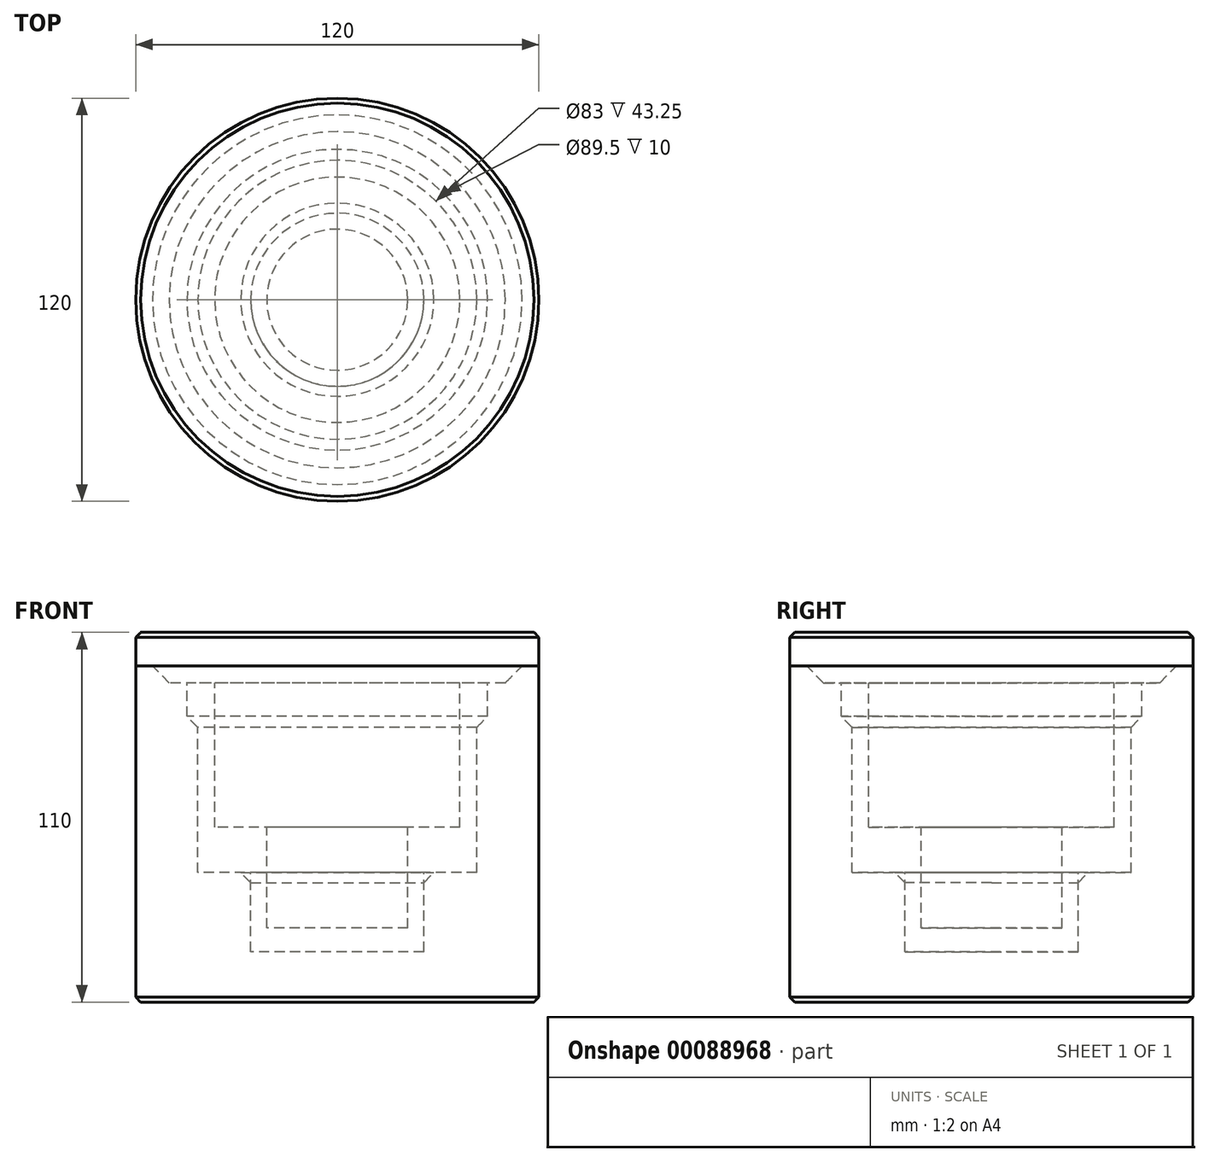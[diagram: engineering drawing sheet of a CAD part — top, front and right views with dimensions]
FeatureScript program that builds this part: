
annotation { "Feature Type Name" : "Feature", "Feature Type Description" : "" }
export const myFeature = defineFeature(function(context is Context, id is Id, definition is map)
    precondition{}
    {
        {
            var Q0;
            Q0=qCreatedBy(makeId("Front.planeOp"),FACE);
            var sketch = newSketch(context, id + "F0", { "sketchPlane" : qUnion([Q0])});
            skLineSegment(sketch, "E0.bottom", {"start": v(60, 47.5) * mm, "end": v(-60, 47.5) * mm});
            skLineSegment(sketch, "E0.top", {"start": v(60, -47.5) * mm, "end": v(-60, -47.5) * mm});
            skLineSegment(sketch, "E0.left", {"start": v(60, 47.5) * mm, "end": v(60, -47.5) * mm});
            skLineSegment(sketch, "E0.right", {"start": v(-60, 47.5) * mm, "end": v(-60, -47.5) * mm});
            skPoint(sketch, "E0.middle", {"position": v(0, 0) * mm});
            skLineSegment(sketch, "E1", {"start": v(0, 121.28) * mm, "end": v(0, -93.9) * mm});
            skLineSegment(sketch, "E2.top", {"start": v(25.75, -32.5) * mm, "end": v(-25.75, -32.5) * mm});
            skLineSegment(sketch, "E2.left", {"start": v(41.5, 32.5) * mm, "end": v(41.5, -9) * mm});
            skLineSegment(sketch, "E2.right", {"start": v(-41.5, 32.5) * mm, "end": v(-41.5, -9) * mm});
            skLineSegment(sketch, "E3", {"start": v(-41.5, 32.5) * mm, "end": v(-41.5, 47.5) * mm});
            skLineSegment(sketch, "E4", {"start": v(41.5, 30.56) * mm, "end": v(41.5, 47.5) * mm});
            skLineSegment(sketch, "E5", {"start": v(-60, 37.5) * mm, "end": v(60, 37.5) * mm});
            skLineSegment(sketch, "E6", {"start": v(-44.75, 47.5) * mm, "end": v(-44.75, 37.5) * mm});
            skLineSegment(sketch, "E7", {"start": v(44.75, 47.5) * mm, "end": v(44.75, 37.5) * mm});
            skLineSegment(sketch, "E8.top", {"start": v(21, -25.5) * mm, "end": v(-21, -25.5) * mm});
            skLineSegment(sketch, "E8.left", {"start": v(36.5, 25.5) * mm, "end": v(36.5, 4.5) * mm});
            skLineSegment(sketch, "E8.right", {"start": v(-36.5, 25.5) * mm, "end": v(-36.5, 4.5) * mm});
            skLineSegment(sketch, "E9", {"start": v(-36.5, 25.5) * mm, "end": v(-36.5, 47.5) * mm});
            skLineSegment(sketch, "E10", {"start": v(36.5, 25.5) * mm, "end": v(36.5, 47.5) * mm});
            skLineSegment(sketch, "E11", {"start": v(-60, 47.5) * mm, "end": v(-60, 62.5) * mm});
            skLineSegment(sketch, "E12", {"start": v(-60, 62.5) * mm, "end": v(60, 62.5) * mm});
            skLineSegment(sketch, "E13", {"start": v(60, 62.5) * mm, "end": v(60, 47.5) * mm});
            skPoint(sketch, "E14.orphan", {"position": v(0, 65.26) * mm});
            skLineSegment(sketch, "E15", {"start": v(-44.75, 37.5) * mm, "end": v(-41.5, 34.25) * mm});
            skPoint(sketch, "E16", {"position": v(-41.5, 40) * mm});
            skPoint(sketch, "E17.end.orphan", {"position": v(-46.38, 47.5) * mm});
            skPoint(sketch, "E18.end.orphan", {"position": v(-60, 52.5) * mm});
            skPoint(sketch, "E19.MirrorCS.end.orphan", {"position": v(46.38, 47.5) * mm});
            skPoint(sketch, "E20.MirrorCS.end.orphan", {"position": v(60, 52.5) * mm});
            skLineSegment(sketch, "E21.top", {"start": v(21, 25.5) * mm, "end": v(-21, 25.5) * mm});
            skLineSegment(sketch, "E21.left", {"start": v(21, -25.5) * mm, "end": v(21, 25.5) * mm});
            skLineSegment(sketch, "E21.right", {"start": v(-21, -25.5) * mm, "end": v(-21, 25.5) * mm});
            skLineSegment(sketch, "E22", {"start": v(-36.5, 4.5) * mm, "end": v(36.5, 4.5) * mm});
            skPoint(sketch, "E23.orphan", {"position": v(-36.5, -25.5) * mm});
            skPoint(sketch, "E24.orphan", {"position": v(36.5, -25.5) * mm});
            skLineSegment(sketch, "E25", {"start": v(-41.5, -9) * mm, "end": v(-25.75, -9) * mm});
            skLineSegment(sketch, "E26", {"start": v(-25.75, -9) * mm, "end": v(-25.75, -32.5) * mm});
            skLineSegment(sketch, "E27.MirrorCS", {"start": v(41.5, -9) * mm, "end": v(25.75, -9) * mm});
            skLineSegment(sketch, "E28.MirrorCS", {"start": v(25.75, -9) * mm, "end": v(25.75, -32.5) * mm});
            skPoint(sketch, "E29.orphan", {"position": v(-41.5, -32.5) * mm});
            skPoint(sketch, "E30.orphan", {"position": v(41.5, -32.5) * mm});
            skLineSegment(sketch, "E31", {"start": v(-60, 52.5) * mm, "end": v(-55, 52.5) * mm});
            skLineSegment(sketch, "E32", {"start": v(-55, 52.5) * mm, "end": v(-50, 47.5) * mm});
            skSolve(sketch);
        }
        {
            var Q0;
            {var subQ4=sQuery(id+"F0.wireOp",EDGE,"E18");Q0=makeQuery(id+"F0.imprint","IMPRINT",FACE,{"disambiguationData":[TD([[makeQuery(id+"F0.imprint","IMPRINT",EDGE,{"derivedFrom":subQ4}),1.0]])]});}
            var Q1;
            {var subQ3=sQuery(id+"F0.wireOp",EDGE,"E6");Q1=makeQuery(id+"F0.imprint","IMPRINT",FACE,{"disambiguationData":[TD([[makeQuery(id+"F0.imprint","IMPRINT",EDGE,{"derivedFrom":subQ3}),-1.0]])]});}
            var Q2;
            {var subQ10=sQuery(id+"F0.wireOp",EDGE,"E15");Q2=makeQuery(id+"F0.imprint","IMPRINT",FACE,{"disambiguationData":[TD([[makeQuery(id+"F0.imprint","IMPRINT",EDGE,{"derivedFrom":subQ10}),-1.0]])]});}
            var Q3;
            {var subQ4=sQuery(id+"F0.wireOp",EDGE,"E31");Q3=makeQuery(id+"F0.imprint","IMPRINT",FACE,{"disambiguationData":[TD([[makeQuery(id+"F0.imprint","IMPRINT",EDGE,{"derivedFrom":subQ4}),-1.0]])]});}
            var Q4;
            Q4=sQuery(id+"F0.wireOp",EDGE,"E1");
            revolve(context, id + "F1", {"entities" : qUnion([Q0, Q1, Q2, Q3]), "axis" : qUnion([Q4]), "revolveType" : RevolveType.FULL});
        }
        {
            var Q0;
            {var subQ9=sQuery(id+"F0.wireOp",EDGE,"E18");Q0=makeQuery(id+"F0.imprint","IMPRINT",FACE,{"disambiguationData":[TD([[makeQuery(id+"F0.imprint","IMPRINT",EDGE,{"derivedFrom":subQ9}),-1.0]])]});}
            var Q1;
            {var subQ0=sQuery(id+"F0.wireOp",EDGE,"E8.right");Q1=makeQuery(id+"F0.imprint","IMPRINT",FACE,{"disambiguationData":[TD([[makeQuery(id+"F0.imprint","IMPRINT",EDGE,{"derivedFrom":subQ0}),1.0]])]});}
            var Q2;
            {var subQ0=sQuery(id+"F0.wireOp",EDGE,"E9");var subQ1=sQuery(id+"F0.wireOp",EDGE,"E0.bottom");var subQ2=makeQuery(id+"F0.imprint","INTERSECT",VERTEX,{"derivedFrom":[subQ1,subQ0]});Q2=makeQuery(id+"F0.imprint","IMPRINT",FACE,{"disambiguationData":[TD([[makeQuery(id+"F0.imprint","IMPRINT",EDGE,{"disambiguationData":[TD([[subQ2,1.0]])],"derivedFrom":subQ1}),1.0]])]});}
            var Q3;
            {var subQ0=sQuery(id+"F0.wireOp",EDGE,"E21.top");var subQ1=sQuery(id+"F0.wireOp",EDGE,"E1");var subQ2=makeQuery(id+"F0.imprint","INTERSECT",VERTEX,{"derivedFrom":[subQ1,subQ0]});Q3=makeQuery(id+"F0.imprint","IMPRINT",FACE,{"disambiguationData":[TD([[makeQuery(id+"F0.imprint","IMPRINT",EDGE,{"disambiguationData":[TD([[subQ2,-1.0]])],"derivedFrom":subQ1}),-1.0]])]});}
            var Q4;
            {var subQ0=sQuery(id+"F0.wireOp",EDGE,"E22");var subQ1=sQuery(id+"F0.wireOp",EDGE,"E1");var subQ2=makeQuery(id+"F0.imprint","INTERSECT",VERTEX,{"derivedFrom":[subQ1,subQ0]});Q4=makeQuery(id+"F0.imprint","IMPRINT",FACE,{"disambiguationData":[TD([[makeQuery(id+"F0.imprint","IMPRINT",EDGE,{"disambiguationData":[TD([[subQ2,-1.0]])],"derivedFrom":subQ1}),-1.0]])]});}
            var Q5;
            {var subQ3=sQuery(id+"F0.wireOp",EDGE,"E31");Q5=makeQuery(id+"F0.imprint","IMPRINT",FACE,{"disambiguationData":[TD([[makeQuery(id+"F0.imprint","IMPRINT",EDGE,{"derivedFrom":subQ3}),1.0]])]});}
            var Q6;
            Q6=sQuery(id+"F0.wireOp",EDGE,"E1");
            revolve(context, id + "F2", {"entities" : qUnion([Q0, Q1, Q2, Q3, Q4, Q5]), "axis" : qUnion([Q6]), "revolveType" : RevolveType.FULL});
        }
        {
            var Q0;
            {var subQ3=sQuery(id+"F0.wireOp",EDGE,"E6");Q0=makeQuery(id+"F0.imprint","IMPRINT",FACE,{"disambiguationData":[TD([[makeQuery(id+"F0.imprint","IMPRINT",EDGE,{"derivedFrom":subQ3}),1.0]])]});}
            var Q1;
            {var subQ0=sQuery(id+"F0.wireOp",EDGE,"E3");var subQ1=sQuery(id+"F0.wireOp",EDGE,"E0.bottom");var subQ2=makeQuery(id+"F0.imprint","INTERSECT",VERTEX,{"derivedFrom":[subQ1,subQ0]});Q1=makeQuery(id+"F0.imprint","IMPRINT",FACE,{"disambiguationData":[TD([[makeQuery(id+"F0.imprint","IMPRINT",EDGE,{"disambiguationData":[TD([[subQ2,1.0]])],"derivedFrom":subQ1}),1.0]])]});}
            var Q2;
            {var subQ1=sQuery(id+"F0.wireOp",EDGE,"E2.right");Q2=makeQuery(id+"F0.imprint","IMPRINT",FACE,{"disambiguationData":[TD([[makeQuery(id+"F0.imprint","IMPRINT",EDGE,{"derivedFrom":subQ1}),1.0]])]});}
            var Q3;
            {var subQ3=sQuery(id+"F0.wireOp",EDGE,"E15");Q3=makeQuery(id+"F0.imprint","IMPRINT",FACE,{"disambiguationData":[TD([[makeQuery(id+"F0.imprint","IMPRINT",EDGE,{"derivedFrom":subQ3}),1.0]])]});}
            var Q4;
            Q4=sQuery(id+"F0.wireOp",EDGE,"E1");
            revolve(context, id + "F3", {"entities" : qUnion([Q0, Q1, Q2, Q3]), "axis" : qUnion([Q4]), "revolveType" : RevolveType.FULL});
        }
        {
            var Q0;
            Q0=makeQuery(id+"F2.opRevolve","SWEPT_EDGE",EDGE,{"disambiguationData":[OSD([sQuery(id+"F0.wireOp",EDGE,"E11"),sQuery(id+"F0.wireOp",EDGE,"E12")])]});
            chamfer(context, id + "F4", {"entities" : qUnion([Q0]), "width" : 1.5 * mm, "tangentPropagation" : true});
        }
        {
            var Q0;
            Q0=makeQuery(id+"F1.opRevolve","SWEPT_EDGE",EDGE,{"disambiguationData":[OSD([sQuery(id+"F0.wireOp",EDGE,"E0.top"),sQuery(id+"F0.wireOp",EDGE,"E0.right")])]});
            chamfer(context, id + "F5", {"entities" : qUnion([Q0]), "width" : 1.5 * mm, "tangentPropagation" : true});
        }
        {
            var Q0;
            Q0=makeQuery(id+"F1.opRevolve","SWEPT_EDGE",EDGE,{"disambiguationData":[OSD([sQuery(id+"F0.wireOp",EDGE,"E25"),sQuery(id+"F0.wireOp",EDGE,"E26")])]});
            chamfer(context, id + "F6", {"entities" : qUnion([Q0]), "width" : 3 * mm, "tangentPropagation" : true});
        }
    });
